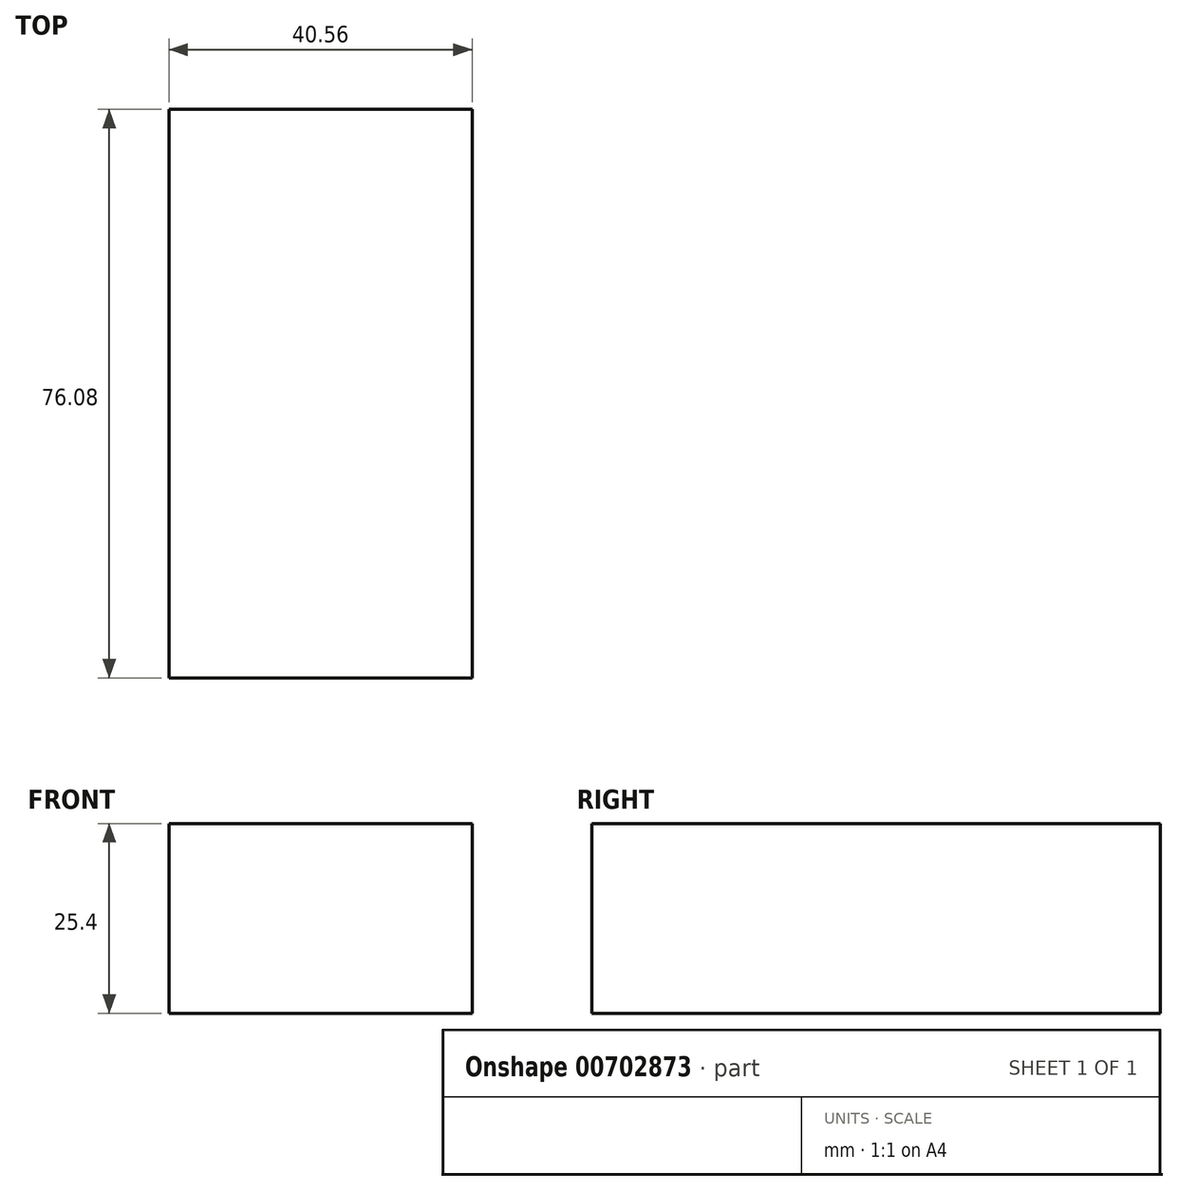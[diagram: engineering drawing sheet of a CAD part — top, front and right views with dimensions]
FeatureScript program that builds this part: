
annotation { "Feature Type Name" : "Feature", "Feature Type Description" : "" }
export const myFeature = defineFeature(function(context is Context, id is Id, definition is map)
    precondition{}
    {
        {
            var Q0;
            Q0=qCreatedBy(makeId("Top.planeOp"),FACE);
            var sketch = newSketch(context, id + "F0", { "sketchPlane" : qUnion([Q0])});
            skLineSegment(sketch, "E0.bottom", {"start": v(20.28, -38.04) * mm, "end": v(-20.28, -38.04) * mm});
            skLineSegment(sketch, "E0.top", {"start": v(20.28, 38.04) * mm, "end": v(-20.28, 38.04) * mm});
            skLineSegment(sketch, "E0.left", {"start": v(20.28, -38.04) * mm, "end": v(20.28, 38.04) * mm});
            skLineSegment(sketch, "E0.right", {"start": v(-20.28, -38.04) * mm, "end": v(-20.28, 38.04) * mm});
            skPoint(sketch, "E0.middle", {"position": v(0, 0) * mm});
            skSolve(sketch);
        }
        {
            var Q0;
            Q0 = qSketchRegion(id + "F0", true);
            extrude(context, id + "F1", {"entities" : qUnion([Q0]), "depth" : 25.4 * mm, "offsetDistance" : 25.4 * mm});
        }
    });
